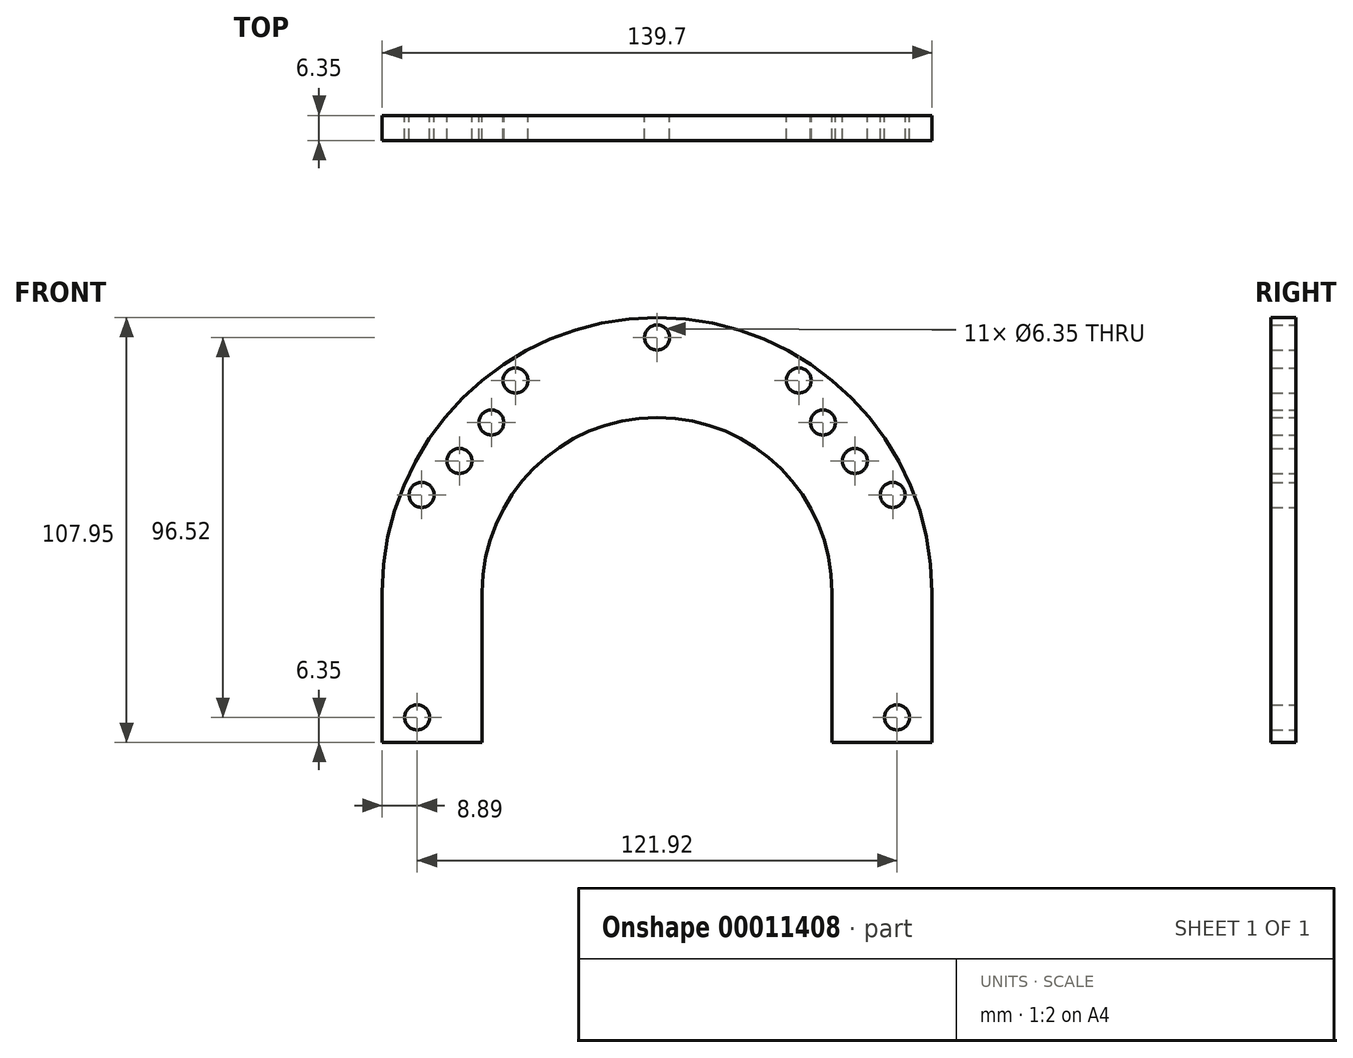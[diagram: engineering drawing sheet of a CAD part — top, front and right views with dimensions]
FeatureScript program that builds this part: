
annotation { "Feature Type Name" : "Feature", "Feature Type Description" : "" }
export const myFeature = defineFeature(function(context is Context, id is Id, definition is map)
    precondition{}
    {
        {
            var Q0;
            Q0=qCreatedBy(makeId("Front.planeOp"),FACE);
            var sketch = newSketch(context, id + "F0", { "sketchPlane" : qUnion([Q0])});
            skCircle(sketch, "E0", {"center": v(0, 0) * mm, "radius": 60.32 * mm, "construction": true});
            skArc(sketch, "E1", {"start": v(69.85, 0) * mm, "mid": v(0, 69.85) * mm, "end": v(-69.85, 0) * mm});
            skCircle(sketch, "E2", {"center": v(0, 0) * mm, "radius": 64.77 * mm, "construction": true});
            skArc(sketch, "E3", {"start": v(44.45, 0) * mm, "mid": v(0, 44.45) * mm, "end": v(-44.45, 0) * mm});
            skLineSegment(sketch, "E4", {"start": v(44.45, 0) * mm, "end": v(44.45, -38.1) * mm});
            skLineSegment(sketch, "E5", {"start": v(44.45, -38.1) * mm, "end": v(69.85, -38.1) * mm});
            skLineSegment(sketch, "E6", {"start": v(69.85, -38.1) * mm, "end": v(69.85, 0) * mm});
            skLineSegment(sketch, "E7", {"start": v(-44.45, 0) * mm, "end": v(-44.45, -38.1) * mm});
            skLineSegment(sketch, "E8", {"start": v(-44.45, -38.1) * mm, "end": v(-69.85, -38.1) * mm});
            skLineSegment(sketch, "E9", {"start": v(-69.85, -38.1) * mm, "end": v(-69.85, 0) * mm});
            skCircle(sketch, "E10", {"center": v(-59.84, 24.79) * mm, "radius": 3.18 * mm});
            skCircle(sketch, "E11.1.0", {"center": v(-35.99, 53.85) * mm, "radius": 3.18 * mm});
            skCircle(sketch, "E11.2.0", {"center": v(0, 64.77) * mm, "radius": 3.18 * mm});
            skCircle(sketch, "E11.3.0", {"center": v(35.98, 53.85) * mm, "radius": 3.18 * mm});
            skCircle(sketch, "E11.4.0", {"center": v(59.84, 24.79) * mm, "radius": 3.18 * mm});
            skLineSegment(sketch, "E11.anchor1", {"start": v(0, 0) * mm, "end": v(-59.84, 24.79) * mm, "construction": true});
            skLineSegment(sketch, "E11.anchor2", {"start": v(0, 0) * mm, "end": v(59.84, 24.79) * mm, "construction": true});
            skCircle(sketch, "E12", {"center": v(-60.96, -31.75) * mm, "radius": 3.18 * mm});
            skCircle(sketch, "E13", {"center": v(60.96, -31.75) * mm, "radius": 3.18 * mm});
            skCircle(sketch, "E14", {"center": v(-42.13, 43.18) * mm, "radius": 3.18 * mm});
            skCircle(sketch, "E15", {"center": v(-50.23, 33.4) * mm, "radius": 3.18 * mm});
            skCircle(sketch, "E16", {"center": v(42.13, 43.18) * mm, "radius": 3.18 * mm});
            skCircle(sketch, "E17", {"center": v(50.23, 33.4) * mm, "radius": 3.18 * mm});
            skSolve(sketch);
        }
        {
            var Q0;
            Q0 = qSketchRegion(id + "F0", true);
            extrude(context, id + "F1", {"entities" : qUnion([Q0]), "depth" : 6.35 * mm});
        }
        {
            var Q0;
            Q0 = qSketchRegion(id + "F0", true);
            extrude(context, id + "F2", {"entities" : qUnion([Q0]), "operationType" : NewBodyOperationType.ADD, "depth" : 6.35 * mm});
        }
    });
